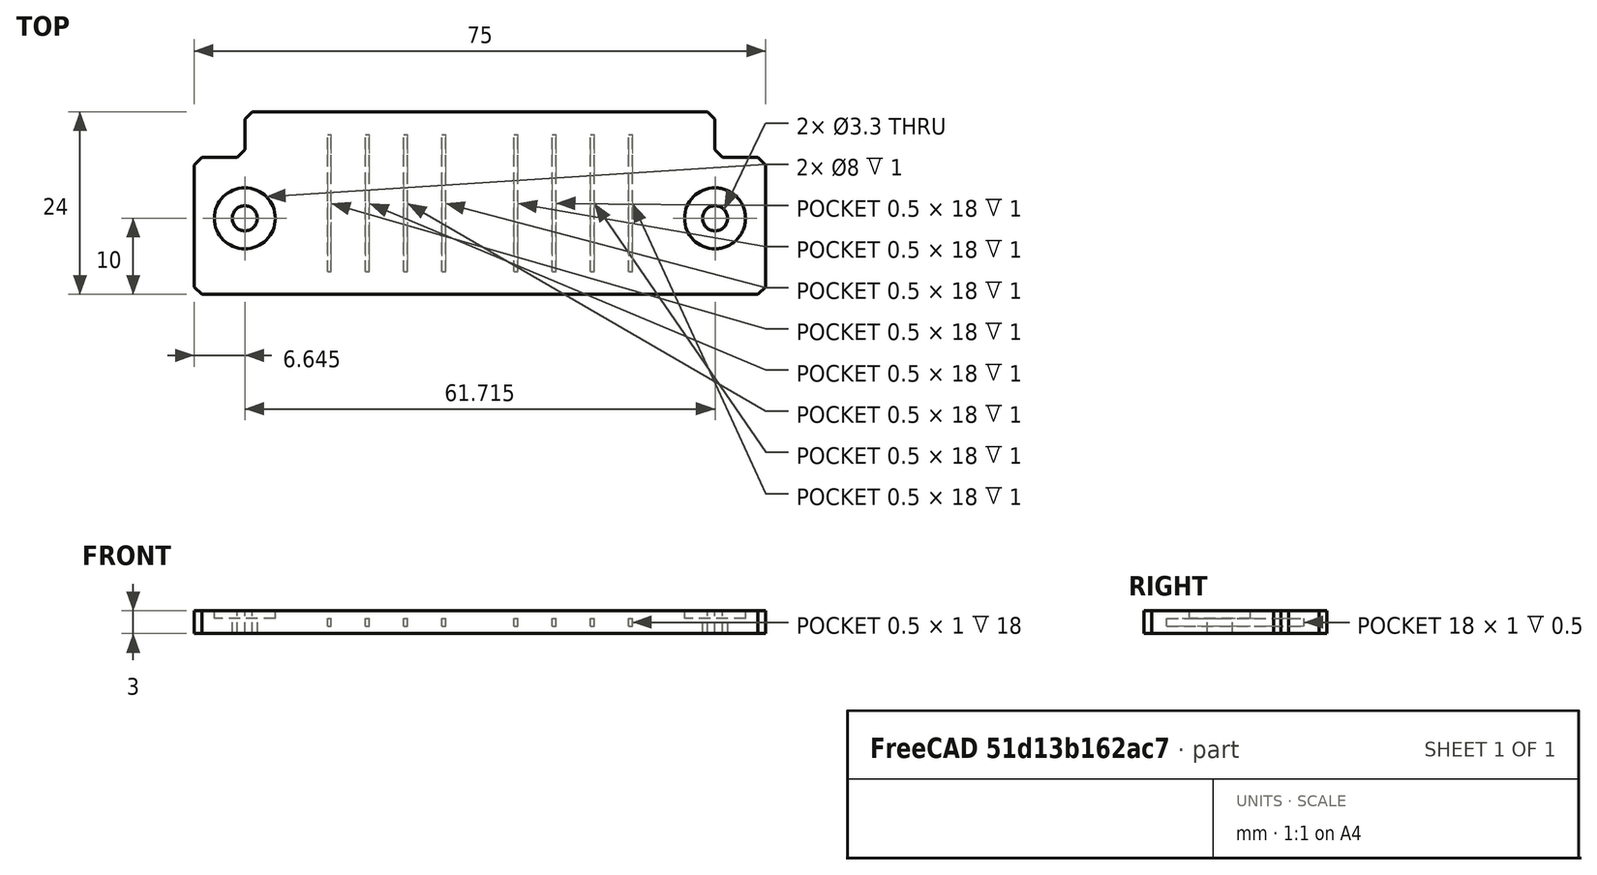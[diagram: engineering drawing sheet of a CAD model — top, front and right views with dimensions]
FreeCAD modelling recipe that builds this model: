
FCSTD DOCUMENT  (FreeCAD 0.18R14555 (Git shallow))
Label: miniitx-case-hdd-bracket
License: All rights reserved
LicenseURL: http://en.wikipedia.org/wiki/All_rights_reserved
objects: Part::Box×10, Part::Cylinder×4, Part::MultiFuse×4, Part::Cut×3, Part::Feature×1, Part::Chamfer×1
note: 23 computed .brp shape members not serialized (recipe doc carries the construction recipe); baked Part::Feature solids carry a one-line shape summary decoded from their .brp

FEATURE [Part::Box] Box  label="Cube"
  AttacherType = Attacher::AttachEngine3D
  Height = 3
  Length = 61.71
  Placement = pos=(-30.855,-10,0) rot=(0,0,1;0rad)
  Width = 24
FEATURE [Part::Cylinder] Cylinder
  Angle = 360
  AttacherType = Attacher::AttachEngine3D
  Height = 10
  Placement = pos=(-30.855,0,0) rot=(0,0,1;0rad)
  Radius = 1.65
FEATURE [Part::Cylinder] Cylinder001
  Angle = 360
  AttacherType = Attacher::AttachEngine3D
  Height = 10
  Placement = pos=(30.86,0,0) rot=(0,0,1;0rad)
  Radius = 1.65
FEATURE [Part::Box] Box001  label="Cube001"
  AttacherType = Attacher::AttachEngine3D
  Height = 3
  Length = 75
  Placement = pos=(-37.5,-10,0) rot=(0,0,1;0rad)
  Width = 18
FEATURE [Part::MultiFuse] Fusion001
  Shapes = -> [Cylinder001,Cylinder]
FEATURE [Part::Cylinder] Cylinder002
  Angle = 360
  AttacherType = Attacher::AttachEngine3D
  Height = 10
  Placement = pos=(-30.855,0,0) rot=(0,0,1;0rad)
  Radius = 4
FEATURE [Part::Cylinder] Cylinder003
  Angle = 360
  AttacherType = Attacher::AttachEngine3D
  Height = 10
  Placement = pos=(30.86,0,0) rot=(0,0,1;0rad)
  Radius = 4
FEATURE [Part::MultiFuse] Fusion002
  Placement = pos=(0,0,2) rot=(0,0,1;0rad)
  Shapes = -> [Cylinder002,Cylinder003]
FEATURE [Part::MultiFuse] Fusion
  Shapes = -> [Box,Box001]
FEATURE [Part::Cut] Cut
  Base = -> Fusion
  Tool = -> Fusion001
FEATURE [Part::Cut] Cut001
  Base = -> Cut
  Tool = -> Fusion002
FEATURE [Part::Box] Box002  label="Cube002"
  AttacherType = Attacher::AttachEngine3D
  Height = 1
  Length = 0.5
  Placement = pos=(-5,-7,1) rot=(0,0,1;0rad)
  Width = 18
FEATURE [Part::Box] Box003  label="Cube003"
  AttacherType = Attacher::AttachEngine3D
  Height = 1
  Length = 0.5
  Placement = pos=(4.5,-7,1) rot=(0,0,1;0rad)
  Width = 18
FEATURE [Part::Box] Box004  label="Cube004"
  AttacherType = Attacher::AttachEngine3D
  Height = 1
  Length = 0.5
  Placement = pos=(9.5,-7,1) rot=(0,0,1;0rad)
  Width = 18
FEATURE [Part::Box] Box005  label="Cube005"
  AttacherType = Attacher::AttachEngine3D
  Height = 1
  Length = 0.5
  Placement = pos=(-10,-7,1) rot=(0,0,1;0rad)
  Width = 18
FEATURE [Part::Box] Box006  label="Cube006"
  AttacherType = Attacher::AttachEngine3D
  Height = 1
  Length = 0.5
  Placement = pos=(-15,-7,1) rot=(0,0,1;0rad)
  Width = 18
FEATURE [Part::Box] Box007  label="Cube007"
  AttacherType = Attacher::AttachEngine3D
  Height = 1
  Length = 0.5
  Placement = pos=(14.5,-7,1) rot=(0,0,1;0rad)
  Width = 18
FEATURE [Part::Box] Box008  label="Cube008"
  AttacherType = Attacher::AttachEngine3D
  Height = 1
  Length = 0.5
  Placement = pos=(19.5,-7,1) rot=(0,0,1;0rad)
  Width = 18
FEATURE [Part::Box] Box009  label="Cube009"
  AttacherType = Attacher::AttachEngine3D
  Height = 1
  Length = 0.5
  Placement = pos=(-20,-7,1) rot=(0,0,1;0rad)
  Width = 18
FEATURE [Part::MultiFuse] Fusion003
  Shapes = -> [Box009,Box003,Box007,Box006,Box004,Box002,Box005,Box008]
FEATURE [Part::Cut] Cut002
  Base = -> Cut001
  Tool = -> Fusion003
FEATURE [Part::Feature] Cut002001  label="Cut003"
  shape: bbox 75 x 24 x 3 mm, 64 faces (baked)
FEATURE [Part::Chamfer] Chamfer
  Base = -> Cut002001
  Edges = 8 edges r=1: [Edge2,Edge4,Edge5,Edge9,Edge12,Edge16,Edge18,Edge20]
